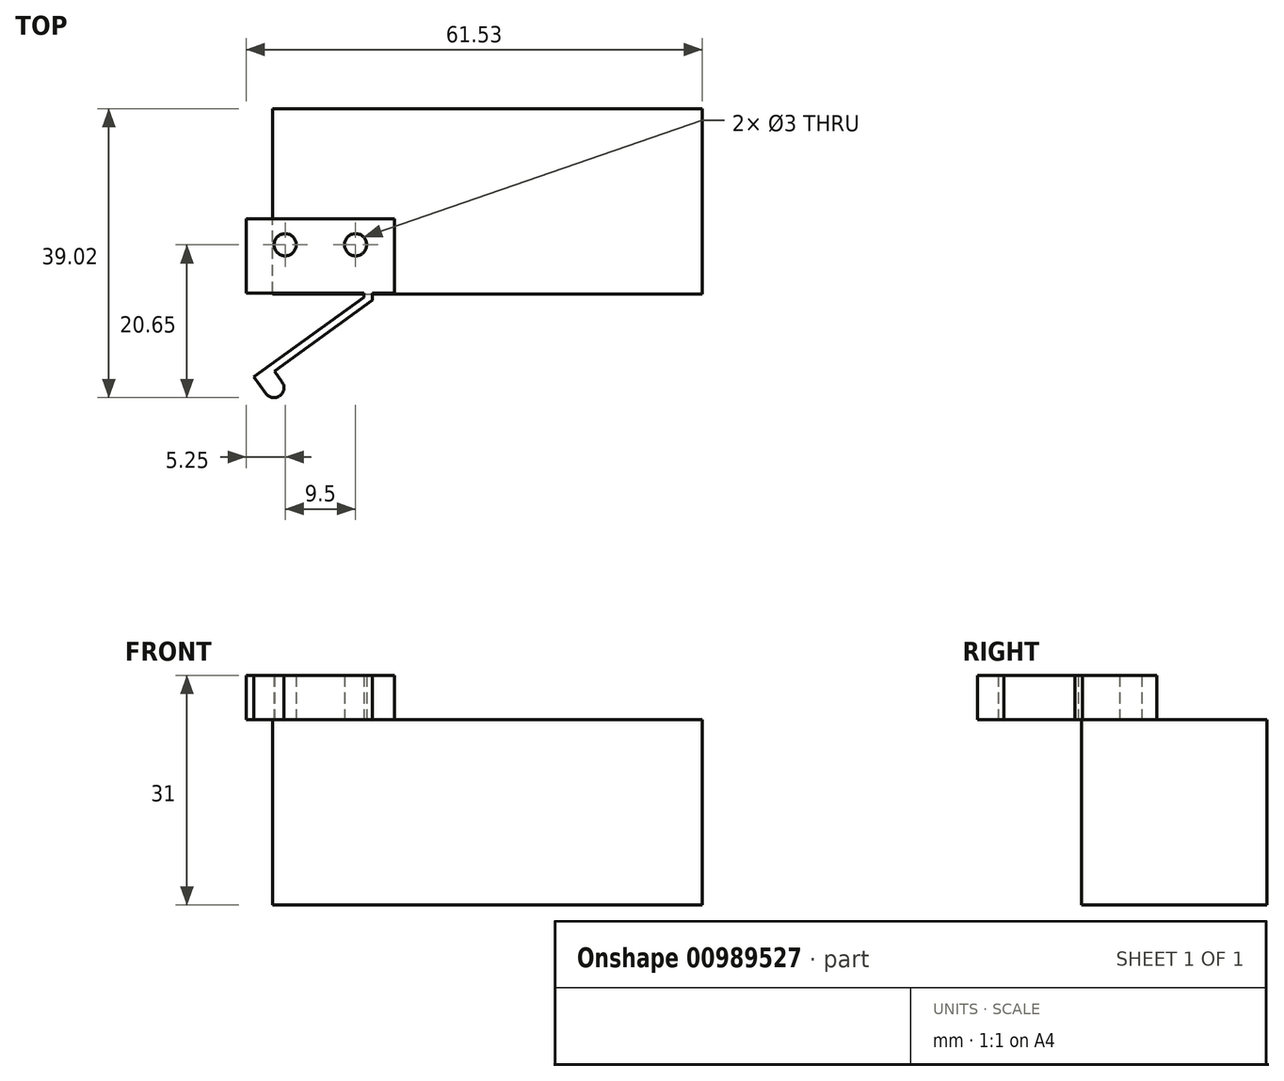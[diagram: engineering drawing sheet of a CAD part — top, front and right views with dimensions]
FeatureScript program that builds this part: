
annotation { "Feature Type Name" : "Feature", "Feature Type Description" : "" }
export const myFeature = defineFeature(function(context is Context, id is Id, definition is map)
    precondition{}
    {
        {
            var Q0;
            Q0=qCreatedBy(makeId("Top.planeOp"),FACE);
            var sketch = newSketch(context, id + "F0", { "sketchPlane" : qUnion([Q0])});
            skLineSegment(sketch, "E0", {"start": v(20, 0) * mm, "end": v(0, 0) * mm});
            skLineSegment(sketch, "E1", {"start": v(0, 0) * mm, "end": v(0, -10) * mm});
            skLineSegment(sketch, "E2", {"start": v(0, -10) * mm, "end": v(20, -10) * mm});
            skLineSegment(sketch, "E3", {"start": v(20, -10) * mm, "end": v(20, 0) * mm});
            skLineSegment(sketch, "E4", {"start": v(17, -10) * mm, "end": v(17, -11) * mm});
            skLineSegment(sketch, "E5", {"start": v(17, -11) * mm, "end": v(1.62, -22.16) * mm});
            skLineSegment(sketch, "E6", {"start": v(1.62, -22.16) * mm, "end": v(1.03, -21.35) * mm});
            skLineSegment(sketch, "E7", {"start": v(1.03, -21.35) * mm, "end": v(15.9, -10.57) * mm});
            skLineSegment(sketch, "E8", {"start": v(15.9, -10.57) * mm, "end": v(15.9, -10) * mm});
            skLineSegment(sketch, "E9", {"start": v(1.62, -22.16) * mm, "end": v(2.66, -23.6) * mm});
            skLineSegment(sketch, "E10", {"start": v(3.8, -20.58) * mm, "end": v(4.83, -22.02) * mm});
            skArc(sketch, "E11", {"start": v(2.66, -23.6) * mm, "mid": v(4.54, -23.9) * mm, "end": v(4.83, -22.02) * mm});
            skCircle(sketch, "E12", {"center": v(14.75, -3.5) * mm, "radius": 1.5 * mm});
            skCircle(sketch, "E13", {"center": v(5.25, -3.5) * mm, "radius": 1.5 * mm});
            skLineSegment(sketch, "E14", {"start": v(2.66, -23.6) * mm, "end": v(4.83, -22.02) * mm, "construction": true});
            skLineSegment(sketch, "E15", {"start": v(5.25, -3.5) * mm, "end": v(0, -3.5) * mm, "construction": true});
            skPoint(sketch, "E15.endSnap0", {"position": v(0, -5) * mm});
            skLineSegment(sketch, "E16", {"start": v(14.75, -3.5) * mm, "end": v(20, -3.5) * mm, "construction": true});
            skSolve(sketch);
        }
        {
            var Q0;
            Q0=makeQuery(id+"F0.imprint","IMPRINT",FACE,{"disambiguationData":[TD([[makeQuery(id+"F0.imprint","IMPRINT",EDGE,{"derivedFrom":sQuery(id+"F0.wireOp",EDGE,"E0")}),1.0]])]});
            var Q1;
            {var subQ1=sQuery(id+"F0.wireOp",EDGE,"E4");Q1=makeQuery(id+"F0.imprint","IMPRINT",FACE,{"disambiguationData":[TD([[makeQuery(id+"F0.imprint","IMPRINT",EDGE,{"derivedFrom":subQ1}),-1.0]])]});}
            var Q2;
            {var subQ0=sQuery(id+"F0.wireOp",EDGE,"E9");Q2=makeQuery(id+"F0.imprint","IMPRINT",FACE,{"disambiguationData":[TD([[makeQuery(id+"F0.imprint","IMPRINT",EDGE,{"derivedFrom":subQ0}),1.0]])]});}
            extrude(context, id + "F1", {"entities" : qUnion([Q0, Q1, Q2]), "endBound" : BoundingType.SYMMETRIC, "depth" : 6 * mm, "offsetDistance" : 25 * mm});
        }
        {
            var Q0;
            Q0=makeQuery(id+"F1.opExtrude","CAP_FACE",FACE,{"disambiguationData":[OSD([sQuery(id+"F0.wireOp",EDGE,"E0"),sQuery(id+"F0.wireOp",EDGE,"E1"),sQuery(id+"F0.wireOp",EDGE,"E2"),sQuery(id+"F0.wireOp",EDGE,"E3"),sQuery(id+"F0.wireOp",EDGE,"E4"),sQuery(id+"F0.wireOp",EDGE,"E5"),sQuery(id+"F0.wireOp",EDGE,"E6"),sQuery(id+"F0.wireOp",EDGE,"E7"),sQuery(id+"F0.wireOp",EDGE,"E8"),sQuery(id+"F0.wireOp",EDGE,"E9"),sQuery(id+"F0.wireOp",EDGE,"E10"),sQuery(id+"F0.wireOp",EDGE,"E11"),sQuery(id+"F0.wireOp",EDGE,"E12"),sQuery(id+"F0.wireOp",EDGE,"E13")])],"isStart":true});
            var sketch = newSketch(context, id + "F2", { "sketchPlane" : qUnion([Q0])});
            skLineSegment(sketch, "E17.bottom", {"start": v(3.53, 10.13) * mm, "end": v(61.53, 10.13) * mm});
            skLineSegment(sketch, "E17.top", {"start": v(3.53, -14.87) * mm, "end": v(61.53, -14.87) * mm});
            skLineSegment(sketch, "E17.left", {"start": v(3.53, 10.13) * mm, "end": v(3.53, -14.87) * mm});
            skLineSegment(sketch, "E17.right", {"start": v(61.53, 10.13) * mm, "end": v(61.53, -14.87) * mm});
            skSolve(sketch);
        }
        {
            var Q0;
            Q0 = qSketchRegion(id + "F2", true);
            extrude(context, id + "F3", {"entities" : qUnion([Q0]), "depth" : 25 * mm, "offsetDistance" : 25 * mm});
        }
    });
